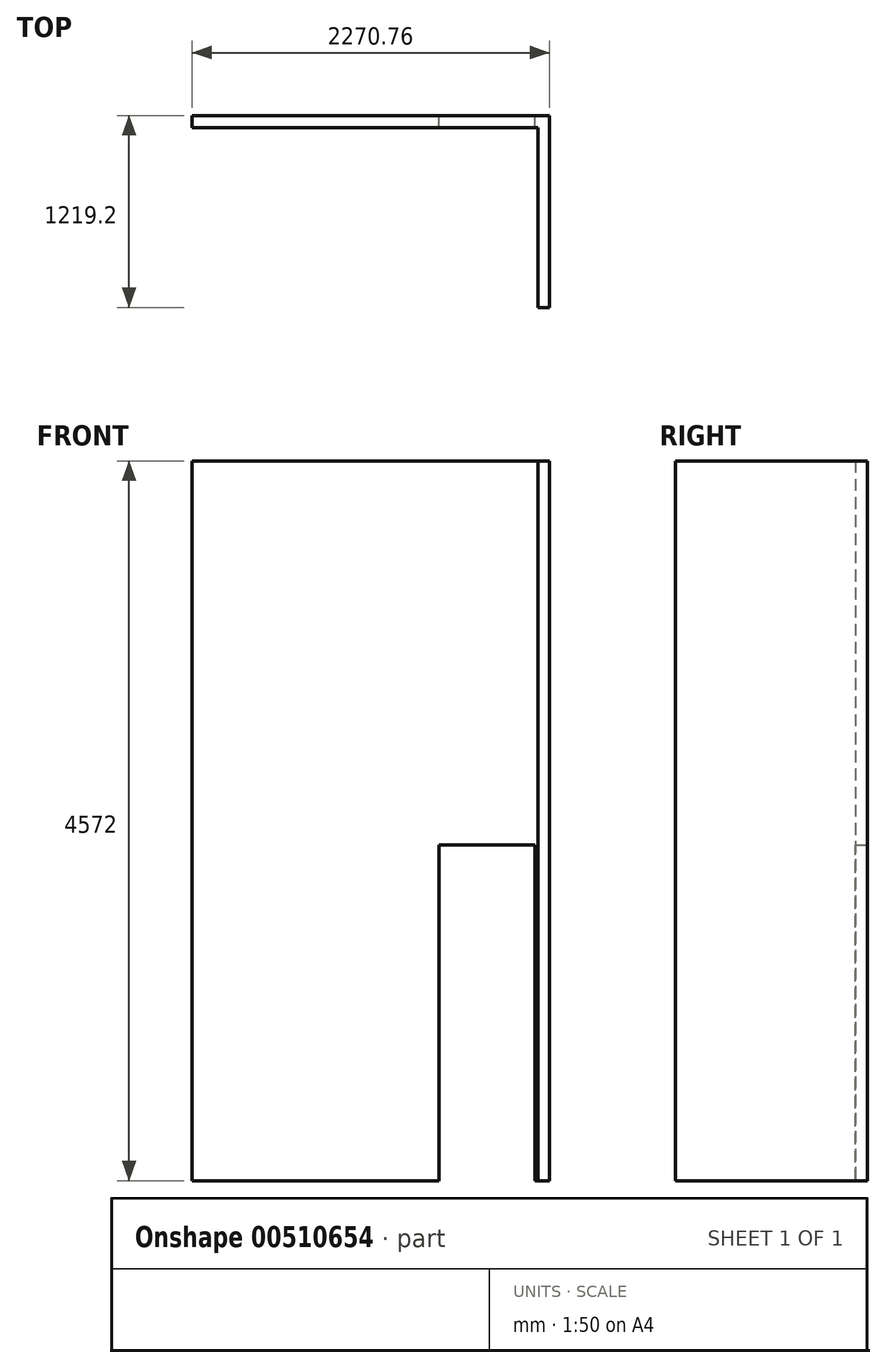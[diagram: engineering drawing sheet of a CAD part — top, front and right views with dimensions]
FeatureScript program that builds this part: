
annotation { "Feature Type Name" : "Feature", "Feature Type Description" : "" }
export const myFeature = defineFeature(function(context is Context, id is Id, definition is map)
    precondition{}
    {
        {
            var Q0;
            Q0=qCreatedBy(makeId("Top.planeOp"),FACE);
            var sketch = newSketch(context, id + "F0", { "sketchPlane" : qUnion([Q0])});
            skLineSegment(sketch, "E0", {"start": v(-733.67, 594.4) * mm, "end": v(1537.1, 594.4) * mm});
            skLineSegment(sketch, "E1", {"start": v(1537.1, 594.4) * mm, "end": v(1537.1, -624.8) * mm});
            skLineSegment(sketch, "E2", {"start": v(1537.1, -624.8) * mm, "end": v(1462.67, -624.8) * mm});
            skLineSegment(sketch, "E3", {"start": v(1462.67, -624.8) * mm, "end": v(1462.67, 518.21) * mm});
            skLineSegment(sketch, "E4", {"start": v(1462.67, 518.21) * mm, "end": v(-731.9, 518.21) * mm});
            skLineSegment(sketch, "E5", {"start": v(-731.9, 518.21) * mm, "end": v(-733.67, 594.4) * mm});
            skSolve(sketch);
        }
        {
            var Q0;
            Q0 = qSketchRegion(id + "F0", true);
            extrude(context, id + "F1", {"entities" : qUnion([Q0]), "depth" : 4572 * mm, "offsetDistance" : 30.48 * mm});
        }
        {
            var Q0;
            Q0=makeQuery(id+"F1.opExtrude","SWEPT_FACE",FACE,{"disambiguationData":[OSD([sQuery(id+"F0.wireOp",EDGE,"E0")])]});
            var sketch = newSketch(context, id + "F2", { "sketchPlane" : qUnion([Q0])});
            skLineSegment(sketch, "E6.bottom", {"start": v(-1445.65, 2133.6) * mm, "end": v(-836.05, 2133.6) * mm});
            skLineSegment(sketch, "E6.top", {"start": v(-1445.65, 0) * mm, "end": v(-836.05, 0) * mm});
            skLineSegment(sketch, "E6.left", {"start": v(-1445.65, 2133.6) * mm, "end": v(-1445.65, 0) * mm});
            skLineSegment(sketch, "E6.right", {"start": v(-836.05, 2133.6) * mm, "end": v(-836.05, 0) * mm});
            skSolve(sketch);
        }
        {
            var Q0;
            Q0 = qSketchRegion(id + "F2", true);
            extrude(context, id + "F3", {"entities" : qUnion([Q0]), "operationType" : NewBodyOperationType.REMOVE, "oppositeDirection" : true, "depth" : 152.4 * mm, "offsetDistance" : 30.48 * mm});
        }
    });
